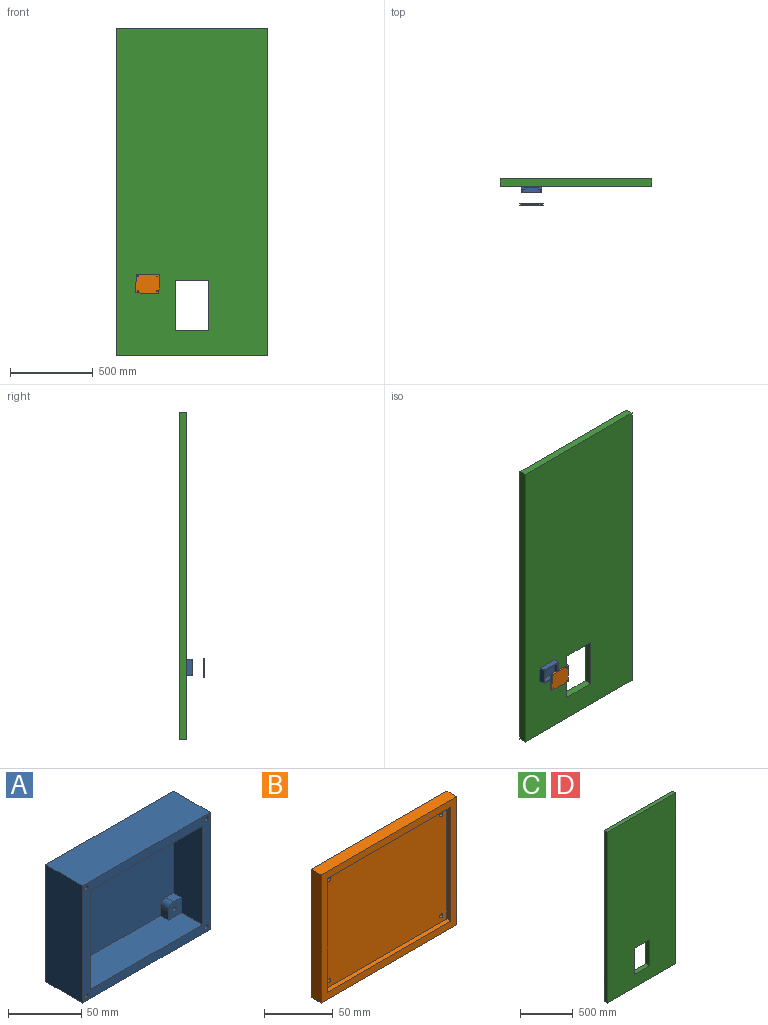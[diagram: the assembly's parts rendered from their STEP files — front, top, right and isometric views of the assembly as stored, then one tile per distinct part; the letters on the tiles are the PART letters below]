
ASSEMBLY  parts=4 mates=3
PART A: 43 faces, bbox 123.2x35.6x97.8 mm
  f0: plane 107.95x82.55mm, normal (0,-1,0), area 8288.3mm2, adj f1,f2,f3,f4,f11,f12,f14,f17
  f1: plane 82.55x27.94mm, normal (1,0,0), area 2112.9mm2, adj f0,f2,f4,f9,f11,f13,f29,f31
  f2: plane 107.95x27.94mm, normal (0,0,1), area 2822.6mm2, adj f0,f1,f3,f9,f27,f28,f30,f31
  f3: plane 82.55x27.94mm, normal (-1,0,0), area 2112.9mm2, adj f0,f2,f4,f9,f17,f19,f26,f27
  f4: plane 107.95x27.94mm, normal (0,0,-1), area 2822.6mm2, adj f0,f1,f3,f9,f12,f13,f18,f19
  f5: plane 97.79x35.56mm, normal (-1,0,0), area 3477.4mm2, adj f6,f8,f9,f10
  f6: plane 123.19x35.56mm, normal (0,0,-1), area 4380.6mm2, adj f5,f7,f9,f10
  f7: plane 97.79x35.56mm, normal (1,0,0), area 3477.4mm2, adj f6,f8,f9,f10
  f8: plane 123.19x35.56mm, normal (0,0,1), area 4380.6mm2, adj f5,f7,f9,f10
  f9: plane 123.19x97.79mm, normal (0,-1,0), area 3086.8mm2, adj f1,f2,f3,f4,f5,f6,f7,f8
  f10: plane 123.19x97.79mm, normal (0,1,0), area 12046.8mm2, adj f5,f6,f7,f8
  f11: plane 7.62x7.62mm, normal (0,0,-1), area 58.1mm2, adj f0,f1,f13,f14
  f12: plane 7.62x7.62mm, normal (1,0,0), area 58.1mm2, adj f0,f4,f13,f14
  f13: plane 12.7x12.7mm, normal (0,-1,0), area 143.6mm2, adj f1,f4,f11,f12,f14,f16
  f14: cylinder r=5.08mm len=7.62mm, axis (0,1,0), area 60.8mm2, adj f0,f11,f12,f13
  f15: cone r=0mm half-angle=59deg, axis (0,-1,0), area 14.2mm2, adj f16
  f16: cylinder r=1.97mm len=5.74mm, axis (0,-1,0), area 71mm2, adj f13,f15
  f17: plane 7.62x7.62mm, normal (0,0,-1), area 58.1mm2, adj f0,f3,f19,f20
  f18: plane 7.62x7.62mm, normal (-1,0,0), area 58.1mm2, adj f0,f4,f19,f20
  f19: plane 12.7x12.7mm, normal (0,-1,0), area 143.6mm2, adj f3,f4,f17,f18,f20,f22
  f20: cylinder r=5.08mm len=7.62mm, axis (0,1,0), area 60.8mm2, adj f0,f17,f18,f19
  f21: cone r=0mm half-angle=59deg, axis (0,-1,0), area 14.2mm2, adj f22
  f22: cylinder r=1.97mm len=5.74mm, axis (0,-1,0), area 71mm2, adj f19,f21
  f23: cone r=0mm half-angle=59deg, axis (0,-1,0), area 14.2mm2, adj f24
  f24: cylinder r=1.97mm len=5.74mm, axis (0,-1,0), area 71mm2, adj f23,f27
  f25: cylinder r=5.08mm len=7.62mm, axis (0,1,0), area 60.8mm2, adj f0,f26,f27,f28
  f26: plane 7.62x7.62mm, normal (0,0,1), area 58.1mm2, adj f0,f3,f25,f27
  f27: plane 12.7x12.7mm, normal (0,-1,0), area 143.6mm2, adj f2,f3,f24,f25,f26,f28
  f28: plane 7.62x7.62mm, normal (-1,0,0), area 58.1mm2, adj f0,f2,f25,f27
  f29: plane 7.62x7.62mm, normal (0,0,1), area 58.1mm2, adj f0,f1,f31,f32
  f30: plane 7.62x7.62mm, normal (1,0,0), area 58.1mm2, adj f0,f2,f31,f32
  f31: plane 12.7x12.7mm, normal (0,-1,0), area 143.6mm2, adj f1,f2,f29,f30,f32,f34
  f32: cylinder r=5.08mm len=7.62mm, axis (0,1,0), area 60.8mm2, adj f0,f29,f30,f31
  f33: cone r=0mm half-angle=59deg, axis (0,-1,0), area 14.2mm2, adj f34
  f34: cylinder r=1.97mm len=5.74mm, axis (0,-1,0), area 71mm2, adj f31,f33
  f35: cone r=0mm half-angle=59deg, axis (0,-1,0), area 14.2mm2, adj f36
  f36: cylinder r=1.97mm len=5.74mm, axis (0,-1,0), area 71mm2, adj f9,f35
  f37: cone r=0mm half-angle=59deg, axis (0,-1,0), area 14.2mm2, adj f38
  f38: cylinder r=1.97mm len=5.74mm, axis (0,-1,0), area 71mm2, adj f9,f37
  f39: cone r=0mm half-angle=59deg, axis (0,-1,0), area 14.2mm2, adj f40
  f40: cylinder r=1.97mm len=5.74mm, axis (0,-1,0), area 71mm2, adj f9,f39
  f41: cone r=0mm half-angle=59deg, axis (0,-1,0), area 14.2mm2, adj f42
  f42: cylinder r=1.97mm len=5.74mm, axis (0,-1,0), area 71mm2, adj f9,f41
PART B: 15 faces, bbox 139.7x10.2x114.3 mm
  f0: plane 114.3x10.16mm, normal (-1,0,0), area 1161.3mm2, adj f1,f3,f4,f5
  f1: plane 139.7x10.16mm, normal (0,0,-1), area 1419.4mm2, adj f0,f2,f4,f5
  f2: plane 114.3x10.16mm, normal (1,0,0), area 1161.3mm2, adj f1,f3,f4,f5
  f3: plane 139.7x10.16mm, normal (0,0,1), area 1419.4mm2, adj f0,f2,f4,f5
  f4: plane 139.7x114.3mm, normal (0,-1,0), area 3064.5mm2, adj f0,f1,f2,f3,f6,f7,f8,f9
  f5: plane 139.7x114.3mm, normal (0,1,0), area 15934.2mm2, adj f0,f1,f2,f3,f11,f12,f13,f14
  f6: plane 101.6x3.81mm, normal (1,0,0), area 387.1mm2, adj f4,f7,f9,f10
  f7: plane 127x3.81mm, normal (0,0,1), area 483.9mm2, adj f4,f6,f8,f10
  f8: plane 101.6x3.81mm, normal (-1,0,0), area 387.1mm2, adj f4,f7,f9,f10
  f9: plane 127x3.81mm, normal (0,0,-1), area 483.9mm2, adj f4,f6,f8,f10
  f10: plane 127x101.6mm, normal (0,-1,0), area 12869.7mm2, adj f6,f7,f8,f9,f11,f12,f13,f14
  f11: cylinder r=1.63mm len=6.35mm, axis (0,1,0), area 65.1mm2, adj f5,f10
  f12: cylinder r=1.63mm len=6.35mm, axis (0,1,0), area 65.1mm2, adj f5,f10
  f13: cylinder r=1.63mm len=6.35mm, axis (0,1,0), area 65.1mm2, adj f5,f10
  f14: cylinder r=1.63mm len=6.35mm, axis (0,1,0), area 65.1mm2, adj f5,f10
PART C: 10 faces, bbox 914.4x44.5x1981.2 mm
  f0: plane 203.2x44.45mm, normal (0,0,1), area 9032.2mm2, adj f1,f7,f8,f9
  f1: plane 304.8x44.45mm, normal (1,0,0), area 13548.4mm2, adj f0,f2,f8,f9
  f2: plane 203.2x44.45mm, normal (0,0,-1), area 9032.2mm2, adj f1,f7,f8,f9
  f3: plane 914.4x44.45mm, normal (0,0,-1), area 40645.1mm2, adj f4,f6,f8,f9
  f4: plane 1981.2x44.45mm, normal (1,0,0), area 88064.3mm2, adj f3,f5,f8,f9
  f5: plane 914.4x44.45mm, normal (0,0,1), area 40645.1mm2, adj f4,f6,f8,f9
  f6: plane 1981.2x44.45mm, normal (-1,0,0), area 88064.3mm2, adj f3,f5,f8,f9
  f7: plane 304.8x44.45mm, normal (-1,0,0), area 13548.4mm2, adj f0,f2,f8,f9
  f8: plane 1981.2x914.4mm, normal (0,-1,0), area 1749673.9mm2, adj f0,f1,f2,f3,f4,f5,f6,f7
  f9: plane 1981.2x914.4mm, normal (0,1,0), area 1749673.9mm2, adj f0,f1,f2,f3,f4,f5,f6,f7
PART D: same geometry as C
PLACE A rot(axis=(0,1,0),0.7deg) t=(188.07,-44.45,436.01)mm
PLACE B rot(axis=(-0.01,0,-1),180deg) t=(188.07,-155.91,436.01)mm
PLACE C at identity fixed
PLACE D at identity
MATE planar C.f8 <-> A.f10  axis (0,-1,0) through (457.2,-44.45,1014.88)mm
MATE cylindrical B.f12 <-> A.f35  axis (0,-1,0) through (130.85,-155.91,481.82)mm
MATE cylindrical B.f11 <-> A.f37  axis (0,-1,0) through (246.41,-155.91,480.37)mm
